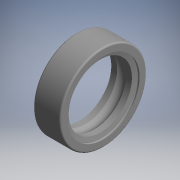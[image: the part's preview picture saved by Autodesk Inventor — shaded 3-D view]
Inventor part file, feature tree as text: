
AUTODESK INVENTOR PART (.ipt)
format: ipt  version: 2017.3 (Build 213256000, 256)  size: 155,648 bytes
history: native  units: mm (DEFAULTED — no unit token found)
features: revolve x1, sketch x1
ambient origin geometry x8: Origin, YZ Plane, XZ Plane, XY Plane, X Axis, Y Axis, Z Axis, Center Point
bodies: Solid1 (feature_tree)
feature tree (2):
  revolve  "Revolution1"  [1 undecoded]
  sketch  "Sketch_22"  dims[d0=360.0deg]
note: 1 required parameter value undecoded (feature->parameter linkage not recoverable at this tier; creation-order binding heuristic only, values carry confidence <= 0.55)
